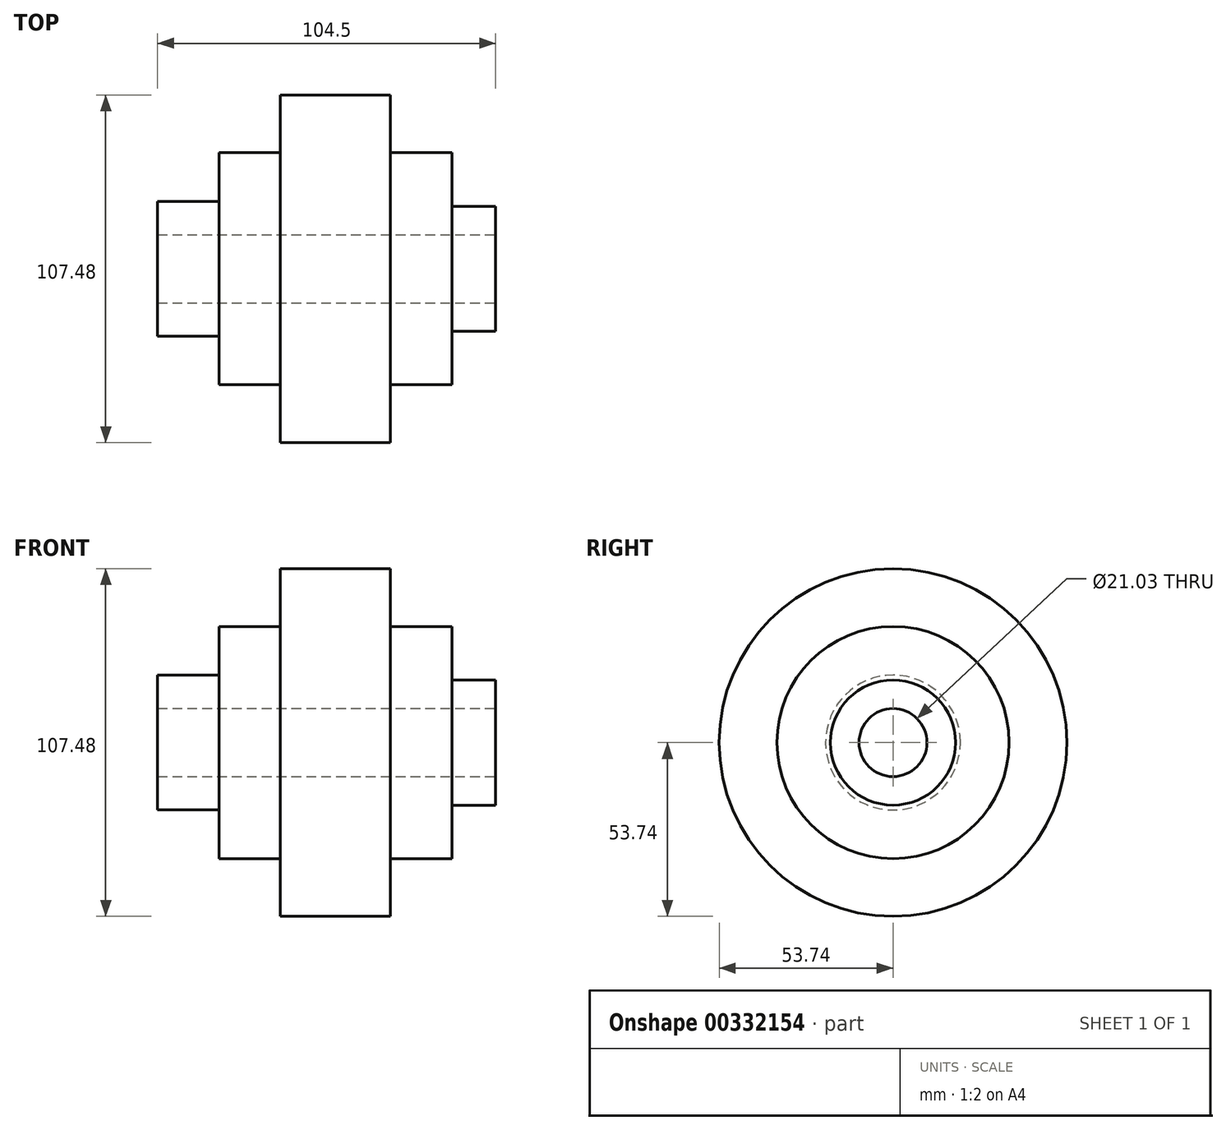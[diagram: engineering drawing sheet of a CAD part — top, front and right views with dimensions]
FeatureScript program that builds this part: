
annotation { "Feature Type Name" : "Feature", "Feature Type Description" : "" }
export const myFeature = defineFeature(function(context is Context, id is Id, definition is map)
    precondition{}
    {
        {
            var Q0;
            Q0=qCreatedBy(makeId("Top.planeOp"),FACE);
            var sketch = newSketch(context, id + "F0", { "sketchPlane" : qUnion([Q0])});
            skLineSegment(sketch, "E0.bottom", {"start": v(-25, 0) * mm, "end": v(25, 0) * mm, "construction": true});
            skLineSegment(sketch, "E0.top", {"start": v(-25, 10) * mm, "end": v(25, 10) * mm});
            skLineSegment(sketch, "E0.left", {"start": v(-25, 0) * mm, "end": v(-25, 10) * mm});
            skLineSegment(sketch, "E0.right", {"start": v(25, 0) * mm, "end": v(25, 10) * mm});
            skLineSegment(sketch, "E1.top", {"start": v(-20, 14) * mm, "end": v(20, 14) * mm});
            skLineSegment(sketch, "E2.bottom", {"start": v(12.5, 18) * mm, "end": v(-12.5, 18) * mm});
            skLineSegment(sketch, "E2.top", {"start": v(12.5, 0) * mm, "end": v(-12.5, 0) * mm});
            skPoint(sketch, "E3", {"position": v(-25, 0) * mm});
            skPoint(sketch, "E4", {"position": v(-92.12, 0) * mm});
            skPoint(sketch, "E5", {"position": v(25, 0) * mm});
            skPoint(sketch, "E6", {"position": v(-74.52, 0) * mm});
            skPoint(sketch, "E7.oppositeSnap0", {"position": v(25, 5) * mm});
            skLineSegment(sketch, "E7.bottom", {"start": v(-25, 0) * mm, "end": v(25, 0) * mm});
            skLineSegment(sketch, "E7.top", {"start": v(-25, 5) * mm, "end": v(25, 5) * mm});
            skLineSegment(sketch, "E7.left", {"start": v(-25, 0) * mm, "end": v(-25, 5) * mm});
            skLineSegment(sketch, "E7.right", {"start": v(25, 0) * mm, "end": v(25, 5) * mm});
            skLineSegment(sketch, "E8", {"start": v(20, 14) * mm, "end": v(20, 5) * mm});
            skLineSegment(sketch, "E9", {"start": v(12.5, 18) * mm, "end": v(12.5, 5) * mm});
            skLineSegment(sketch, "E10", {"start": v(-12.5, 18) * mm, "end": v(-12.5, 5) * mm});
            skLineSegment(sketch, "E11", {"start": v(-20, 14) * mm, "end": v(-20, 5) * mm});
            skLineSegment(sketch, "E12.MirrorCS", {"start": v(60.01, 14) * mm, "end": v(60.01, 5) * mm});
            skSolve(sketch);
        }
        {
            var Q0;
            Q0=sQuery(id+"F0.wireOp",EDGE,"E0.left");
            var Q1;
            Q1=sQuery(id+"F0.wireOp",EDGE,"E0.top");
            var Q2;
            Q2=sQuery(id+"F0.wireOp",EDGE,"E0.right");
            var Q3;
            Q3=sQuery(id+"F0.wireOp",EDGE,"E0.bottom");
            revolve(context, id + "F1", {"bodyType" : ToolBodyType.SURFACE, "surfaceEntities" : qUnion([Q0, Q1, Q2]), "axis" : qUnion([Q3]), "revolveType" : RevolveType.FULL});
        }
        {
            var Q0;
            Q0=sQuery(id+"F0.wireOp",EDGE,"E1.top");
            var Q1;
            Q1=sQuery(id+"F0.wireOp",EDGE,"E1.left");
            var Q2;
            Q2=sQuery(id+"F0.wireOp",EDGE,"E1.right");
            var Q3;
            Q3=sQuery(id+"F0.wireOp",EDGE,"E0.bottom");
            revolve(context, id + "F2", {"bodyType" : ToolBodyType.SURFACE, "surfaceEntities" : qUnion([Q0, Q1, Q2]), "axis" : qUnion([Q3]), "revolveType" : RevolveType.FULL});
        }
        {
            var Q0;
            Q0=sQuery(id+"F0.wireOp",EDGE,"E2.right");
            var Q1;
            Q1=sQuery(id+"F0.wireOp",EDGE,"E2.bottom");
            var Q2;
            Q2=sQuery(id+"F0.wireOp",EDGE,"E2.left");
            var Q3;
            Q3=sQuery(id+"F0.wireOp",EDGE,"E0.bottom");
            revolve(context, id + "F3", {"bodyType" : ToolBodyType.SURFACE, "surfaceEntities" : qUnion([Q0, Q1, Q2]), "axis" : qUnion([Q3]), "revolveType" : RevolveType.FULL});
        }
        {
            var Q0;
            Q0=qCreatedBy(makeId("Top.planeOp"),FACE);
            var sketch = newSketch(context, id + "F4", { "sketchPlane" : qUnion([Q0])});
            skLineSegment(sketch, "E13", {"start": v(-61.69, 0) * mm, "end": v(-151.99, 0) * mm, "construction": true});
            skLineSegment(sketch, "E14", {"start": v(-49.22, 10.51) * mm, "end": v(-153.72, 10.51) * mm});
            skLineSegment(sketch, "E15", {"start": v(-153.72, 10.51) * mm, "end": v(-153.72, 20.85) * mm});
            skLineSegment(sketch, "E16", {"start": v(-153.72, 20.85) * mm, "end": v(-134.74, 20.85) * mm});
            skLineSegment(sketch, "E17", {"start": v(-134.74, 20.85) * mm, "end": v(-134.74, 35.89) * mm});
            skLineSegment(sketch, "E18", {"start": v(-134.74, 35.89) * mm, "end": v(-115.75, 35.89) * mm});
            skLineSegment(sketch, "E19", {"start": v(-115.75, 35.89) * mm, "end": v(-115.75, 53.74) * mm});
            skLineSegment(sketch, "E20", {"start": v(-115.75, 53.74) * mm, "end": v(-81.74, 53.74) * mm});
            skLineSegment(sketch, "E21", {"start": v(-81.74, 53.74) * mm, "end": v(-81.74, 35.89) * mm});
            skLineSegment(sketch, "E22", {"start": v(-81.74, 35.89) * mm, "end": v(-62.75, 35.89) * mm});
            skLineSegment(sketch, "E23", {"start": v(-62.75, 35.89) * mm, "end": v(-62.75, 19.35) * mm});
            skLineSegment(sketch, "E24", {"start": v(-62.75, 19.35) * mm, "end": v(-49.22, 19.35) * mm});
            skLineSegment(sketch, "E25", {"start": v(-49.22, 19.35) * mm, "end": v(-49.22, 10.51) * mm});
            skSolve(sketch);
        }
        {
            var Q0;
            Q0=makeQuery(id+"F4.imprint","IMPRINT",FACE,{"disambiguationData":[TD([[makeQuery(id+"F4.imprint","IMPRINT",EDGE,{"derivedFrom":sQuery(id+"F4.wireOp",EDGE,"E14")}),-1.0]])]});
            var Q1;
            Q1=sQuery(id+"F4.wireOp",EDGE,"E13");
            revolve(context, id + "F5", {"entities" : qUnion([Q0]), "axis" : qUnion([Q1]), "revolveType" : RevolveType.FULL});
        }
    });
